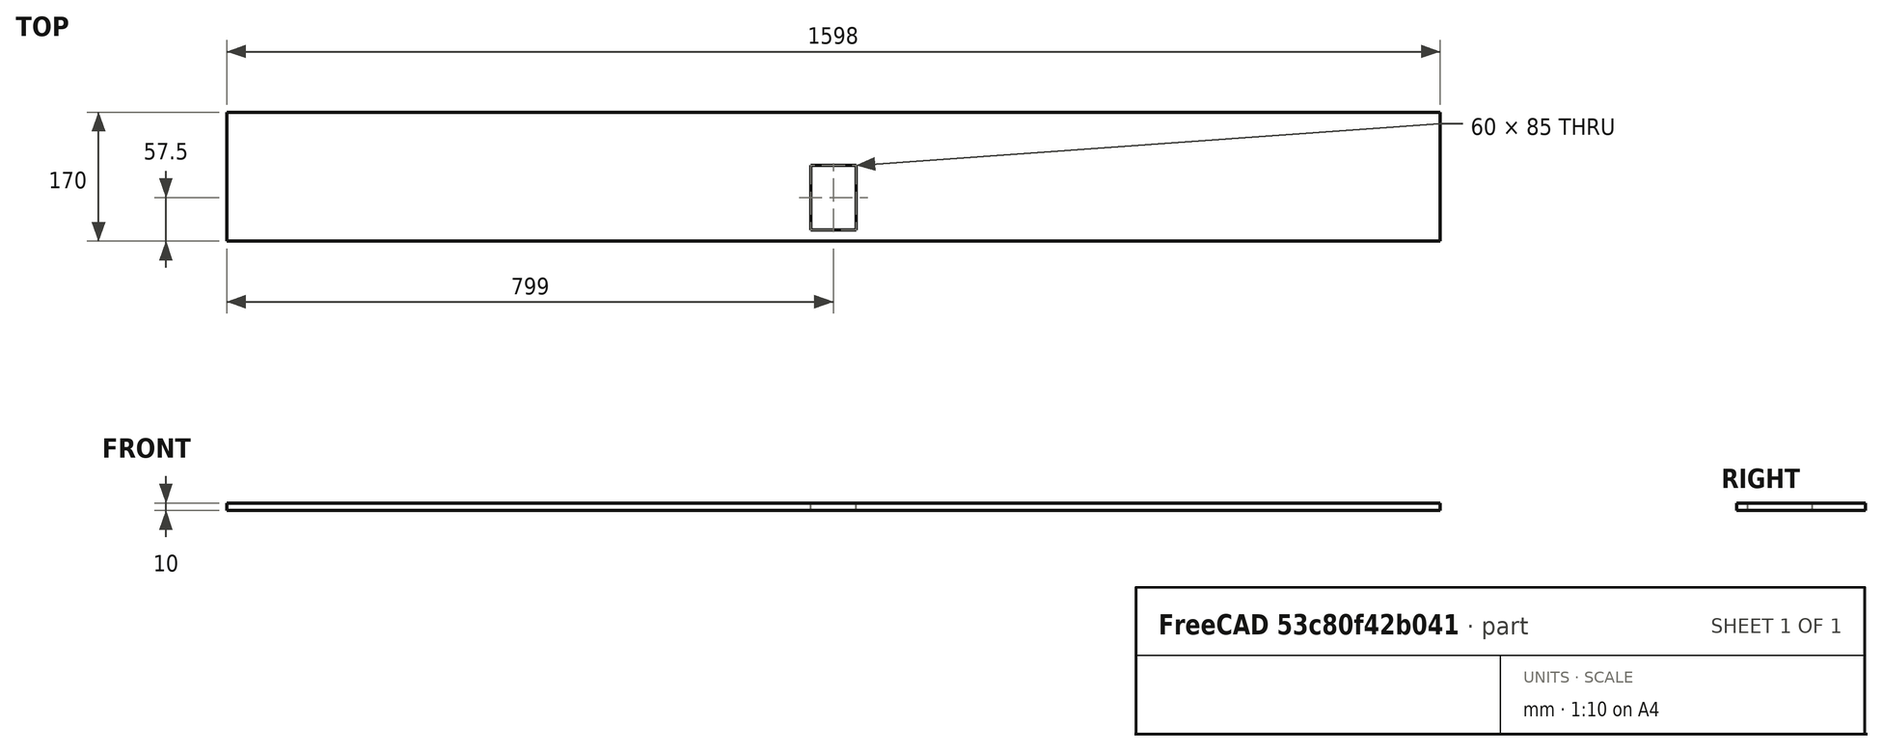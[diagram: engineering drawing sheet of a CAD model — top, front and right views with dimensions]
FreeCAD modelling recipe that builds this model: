
FCSTD DOCUMENT  (FreeCAD 1.0R39319 (Git))
Label: comp23_16mm_plate
License: All rights reserved
LicenseURL: https://en.wikipedia.org/wiki/All_rights_reserved
objects: Sketcher::SketchObject×1, PartDesign::Pad×1, PartDesign::Body×1
note: 6 computed .brp shape members not serialized (recipe doc carries the construction recipe); baked Part::Feature solids carry a one-line shape summary decoded from their .brp

FEATURE [Sketcher::SketchObject] Sketch
  ArcFitTolerance = 1e-06
  AttachmentSupport = -> [XY_Plane]
  FullyConstrained = true
  MakeInternals = false
  MapMode = 5
  sketch-geometry (8):
    g0: LineSegment StartX=0 StartY=0 StartZ=0 EndX=1598 EndY=0 EndZ=0
    g1: LineSegment StartX=1598 StartY=0 StartZ=0 EndX=1598 EndY=170 EndZ=0
    g2: LineSegment StartX=1598 StartY=170 StartZ=0 EndX=0 EndY=170 EndZ=0
    g3: LineSegment StartX=0 StartY=170 StartZ=0 EndX=0 EndY=0 EndZ=0
    g4: LineSegment StartX=769 StartY=100 StartZ=0 EndX=769 EndY=15 EndZ=0
    g5: LineSegment StartX=769 StartY=15 StartZ=0 EndX=829 EndY=15 EndZ=0
    g6: LineSegment StartX=829 StartY=15 StartZ=0 EndX=829 EndY=100 EndZ=0
    g7: LineSegment StartX=829 StartY=100 StartZ=0 EndX=769 EndY=100 EndZ=0
  constraints (23):
    c: Coincident(g0,g1)
    c: Coincident(g1,g2)
    c: Coincident(g2,g3)
    c: Coincident(g3,g0)
    c: Horizontal(g0)
    c: Horizontal(g2)
    c: Vertical(g1)
    c: Vertical(g3)
    c: Coincident(g0,g-1)
    c: DistanceX(g0,g0) = 1598
    c: DistanceY(g3,g3) = 170
    c: Coincident(g4,g5)
    c: Coincident(g5,g6)
    c: Coincident(g6,g7)
    c: Coincident(g7,g4)
    c: Vertical(g4)
    c: Vertical(g6)
    c: Horizontal(g5)
    c: Horizontal(g7)
    c: DistanceX(g7,g7) = 60
    c: DistanceY(g6,g6) = 85
    c: Distance(g3,g4) = 769
    c: Distance(g0,g5) = 15
FEATURE [PartDesign::Pad] Pad
  Direction = (0,0,1)
  Length = 10
  Length2 = 10
  Profile = -> Sketch
  ReferenceAxis = -> Sketch [N_Axis]
  Refine = true
  Suppressed = false
  Type = 0
FEATURE [PartDesign::Body] Body
  AllowCompound = false
  Group = -> [Sketch,Pad]
  Origin = -> Origin
  Tip = -> Pad
